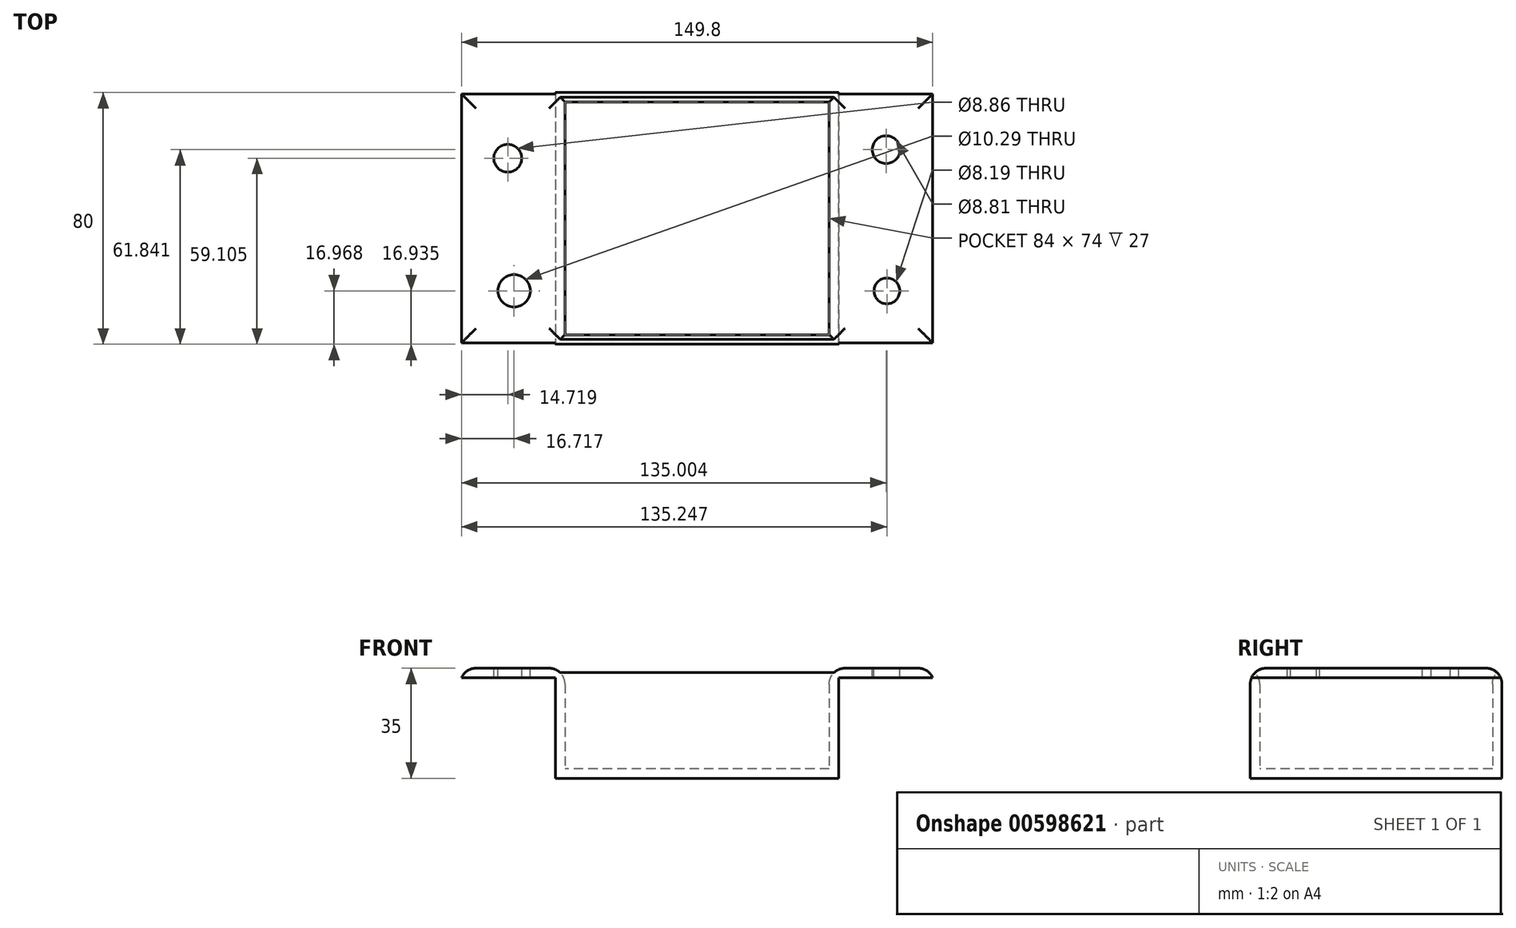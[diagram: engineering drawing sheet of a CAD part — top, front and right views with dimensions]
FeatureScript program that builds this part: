
annotation { "Feature Type Name" : "Feature", "Feature Type Description" : "" }
export const myFeature = defineFeature(function(context is Context, id is Id, definition is map)
    precondition{}
    {
        {
            var Q0;
            Q0=qCreatedBy(makeId("Top.planeOp"),FACE);
            var sketch = newSketch(context, id + "F0", { "sketchPlane" : qUnion([Q0])});
            skLineSegment(sketch, "E0.bottom", {"start": v(45, 40) * mm, "end": v(-45, 40) * mm});
            skLineSegment(sketch, "E0.top", {"start": v(45, -40) * mm, "end": v(-45, -40) * mm});
            skLineSegment(sketch, "E0.left", {"start": v(45, 40) * mm, "end": v(45, -40) * mm});
            skLineSegment(sketch, "E0.right", {"start": v(-45, 40) * mm, "end": v(-45, -40) * mm});
            skPoint(sketch, "E0.middle", {"position": v(0, 0) * mm});
            skSolve(sketch);
        }
        {
            var Q0;
            Q0=makeQuery(id+"F0.imprint","IMPRINT",FACE,{"disambiguationData":[TD([[makeQuery(id+"F0.imprint","IMPRINT",EDGE,{"derivedFrom":sQuery(id+"F0.wireOp",EDGE,"E0.bottom")}),1.0]])]});
            extrude(context, id + "F1", {"entities" : qUnion([Q0]), "depth" : 35 * mm, "offsetDistance" : 25.4 * mm});
        }
        {
            var Q0;
            Q0=makeQuery(id+"F1.opExtrude","CAP_FACE",FACE,{"disambiguationData":[OSD([sQuery(id+"F0.wireOp",EDGE,"E0.bottom"),sQuery(id+"F0.wireOp",EDGE,"E0.top"),sQuery(id+"F0.wireOp",EDGE,"E0.left"),sQuery(id+"F0.wireOp",EDGE,"E0.right")])],"isStart":false});
            shell(context, id + "F2", {"entities" : qUnion([Q0]), "thickness" : 3 * mm});
        }
        {
            var Q0;
            Q0=makeQuery(id+"F1.opExtrude","SWEPT_FACE",FACE,{"disambiguationData":[OSD([sQuery(id+"F0.wireOp",EDGE,"E0.left")])]});
            var sketch = newSketch(context, id + "F3", { "sketchPlane" : qUnion([Q0])});
            skLineSegment(sketch, "E1.bottom", {"start": v(-40, 35) * mm, "end": v(40, 35) * mm});
            skLineSegment(sketch, "E1.top", {"start": v(-40, 32) * mm, "end": v(40, 32) * mm});
            skLineSegment(sketch, "E1.left", {"start": v(-40, 35) * mm, "end": v(-40, 32) * mm});
            skLineSegment(sketch, "E1.right", {"start": v(40, 35) * mm, "end": v(40, 32) * mm});
            skSolve(sketch);
        }
        {
            var Q0;
            Q0=makeQuery(id+"F3.imprint","IMPRINT",FACE,{"disambiguationData":[TD([[makeQuery(id+"F3.imprint","IMPRINT",EDGE,{"derivedFrom":sQuery(id+"F3.wireOp",EDGE,"E1.bottom")}),1.0]])]});
            extrude(context, id + "F4", {"entities" : qUnion([Q0]), "operationType" : NewBodyOperationType.ADD, "depth" : 29.9 * mm, "offsetDistance" : 25.4 * mm});
        }
        {
            var Q0;
            Q0=makeQuery(id+"F1.opExtrude","SWEPT_FACE",FACE,{"disambiguationData":[OSD([sQuery(id+"F0.wireOp",EDGE,"E0.right")])]});
            var sketch = newSketch(context, id + "F5", { "sketchPlane" : qUnion([Q0])});
            skLineSegment(sketch, "E2.bottom", {"start": v(-40, 35) * mm, "end": v(40, 35) * mm});
            skLineSegment(sketch, "E2.top", {"start": v(-40, 32) * mm, "end": v(40, 32) * mm});
            skLineSegment(sketch, "E2.left", {"start": v(-40, 35) * mm, "end": v(-40, 32) * mm});
            skLineSegment(sketch, "E2.right", {"start": v(40, 35) * mm, "end": v(40, 32) * mm});
            skSolve(sketch);
        }
        {
            var Q0;
            Q0 = qSketchRegion(id + "F5", true);
            extrude(context, id + "F6", {"entities" : qUnion([Q0]), "operationType" : NewBodyOperationType.ADD, "depth" : 29.9 * mm, "offsetDistance" : 25 * mm});
        }
        {
            var Q0;
            Q0=makeQuery(id+"F6.boolean.opBoolean","MERGE",FACE,{"derivedFrom":[makeQuery(id+"F4.boolean.opBoolean","MERGE",FACE,{"derivedFrom":[makeQuery(id+"F1.opExtrude","CAP_FACE",FACE,{"disambiguationData":[OSD([sQuery(id+"F0.wireOp",EDGE,"E0.bottom"),sQuery(id+"F0.wireOp",EDGE,"E0.top"),sQuery(id+"F0.wireOp",EDGE,"E0.left"),sQuery(id+"F0.wireOp",EDGE,"E0.right")])],"isStart":false}),makeQuery(id+"F4.opExtrude","SWEPT_FACE",FACE,{"disambiguationData":[OSD([sQuery(id+"F3.wireOp",EDGE,"E1.bottom")])]})]}),makeQuery(id+"F6.opExtrude","SWEPT_FACE",FACE,{"disambiguationData":[OSD([sQuery(id+"F5.wireOp",EDGE,"E2.bottom")])]})]});
            var sketch = newSketch(context, id + "F7", { "sketchPlane" : qUnion([Q0])});
            skCircle(sketch, "E3", {"center": v(60.35, -23.07) * mm, "radius": 4.1 * mm});
            skCircle(sketch, "E4", {"center": v(60.1, 21.84) * mm, "radius": 4.4 * mm});
            skCircle(sketch, "E5", {"center": v(-60.18, 19.1) * mm, "radius": 4.43 * mm});
            skCircle(sketch, "E6", {"center": v(-58.18, -23.03) * mm, "radius": 5.15 * mm});
            skSolve(sketch);
        }
        {
            var Q0;
            Q0=makeQuery(id+"F6.boolean.opBoolean","MERGE",FACE,{"derivedFrom":[makeQuery(id+"F4.boolean.opBoolean","MERGE",FACE,{"derivedFrom":[makeQuery(id+"F1.opExtrude","CAP_FACE",FACE,{"disambiguationData":[OSD([sQuery(id+"F0.wireOp",EDGE,"E0.bottom"),sQuery(id+"F0.wireOp",EDGE,"E0.top"),sQuery(id+"F0.wireOp",EDGE,"E0.left"),sQuery(id+"F0.wireOp",EDGE,"E0.right")])],"isStart":false}),makeQuery(id+"F4.opExtrude","SWEPT_FACE",FACE,{"disambiguationData":[OSD([sQuery(id+"F3.wireOp",EDGE,"E1.bottom")])]})]}),makeQuery(id+"F6.opExtrude","SWEPT_FACE",FACE,{"disambiguationData":[OSD([sQuery(id+"F5.wireOp",EDGE,"E2.bottom")])]})]});
            fillet(context, id + "F8", {"entities" : qUnion([Q0]), "radius" : 5 * mm, "tangentPropagation" : true, "allowEdgeOverflow" : false});
        }
        {
            var Q0;
            Q0 = qSketchRegion(id + "F7", true);
            extrude(context, id + "F9", {"entities" : qUnion([Q0]), "operationType" : NewBodyOperationType.REMOVE, "oppositeDirection" : true, "depth" : 5 * mm, "offsetDistance" : 25 * mm});
        }
    });
